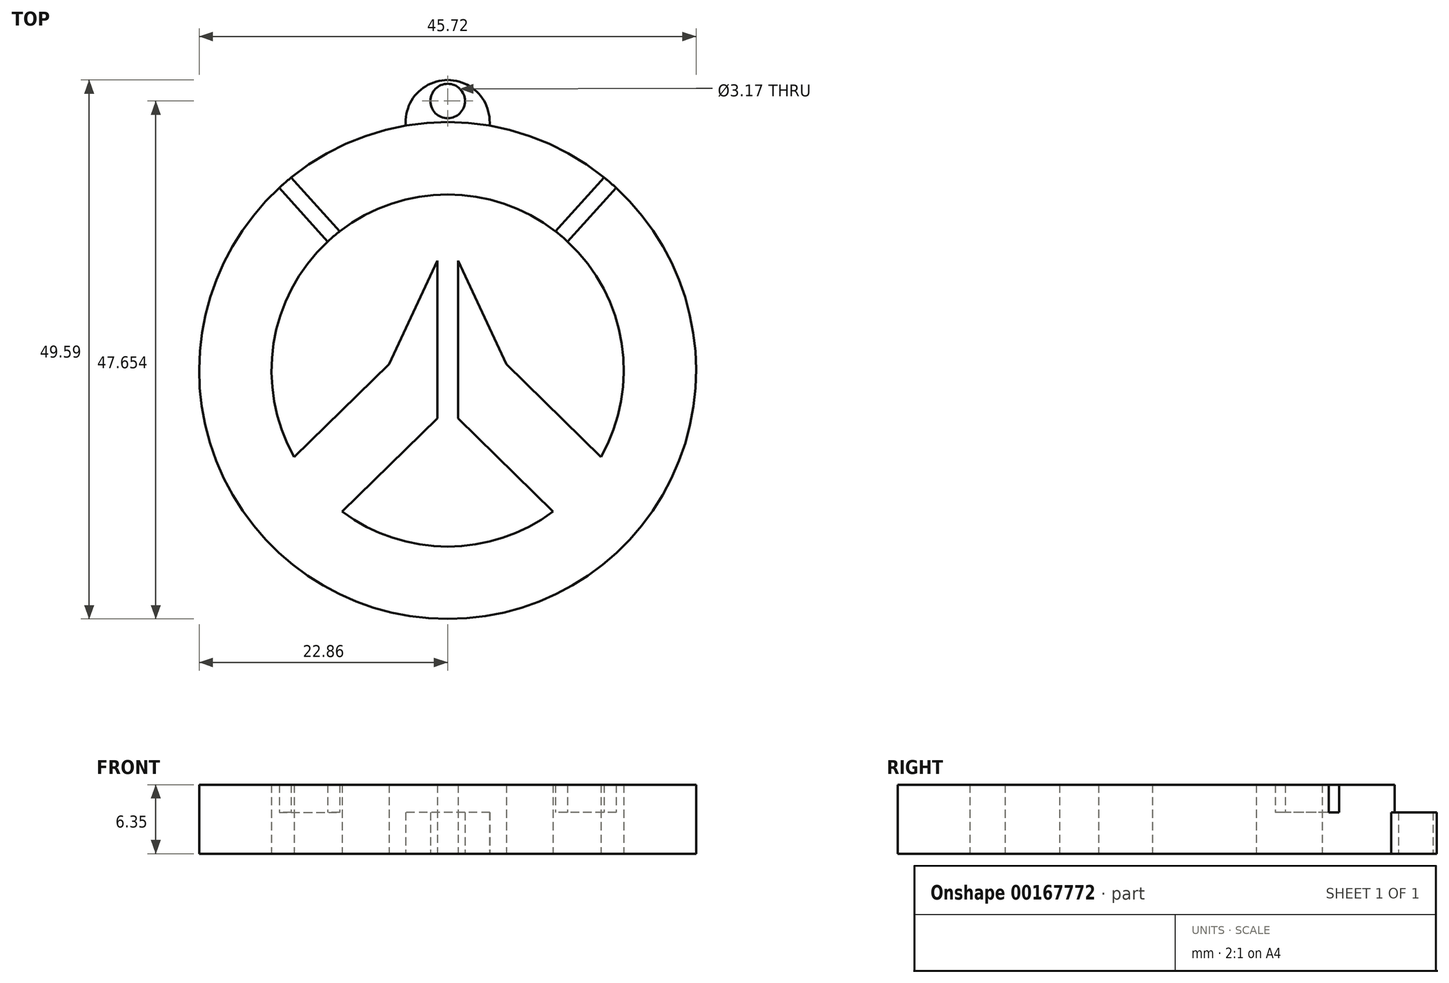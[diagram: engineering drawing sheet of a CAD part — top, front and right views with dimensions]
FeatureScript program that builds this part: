
annotation { "Feature Type Name" : "Feature", "Feature Type Description" : "" }
export const myFeature = defineFeature(function(context is Context, id is Id, definition is map)
    precondition{}
    {
        {
            var Q0;
            Q0=qCreatedBy(makeId("Top.planeOp"),FACE);
            var sketch = newSketch(context, id + "F0", { "sketchPlane" : qUnion([Q0])});
            skArc(sketch, "E0", {"start": v(-3.2, 22.5) * mm, "mid": v(-26.07, -0.35) * mm, "end": v(-3.2, -23.21) * mm});
            skArc(sketch, "E1", {"start": v(-3.2, 15.85) * mm, "mid": v(-17.2, 7.82) * mm, "end": v(-17.32, -8.32) * mm});
            skLineSegment(sketch, "E2", {"start": v(-4.15, 9.77) * mm, "end": v(-4.15, -4.75) * mm});
            skLineSegment(sketch, "E3", {"start": v(-4.15, -4.75) * mm, "end": v(-12.9, -13.33) * mm});
            skLineSegment(sketch, "E4", {"start": v(-17.32, -8.32) * mm, "end": v(-8.6, 0.23) * mm});
            skLineSegment(sketch, "E5", {"start": v(-8.6, 0.23) * mm, "end": v(-4.15, 9.77) * mm});
            skArc(sketch, "E6.trimOffspring", {"start": v(-12.9, -13.33) * mm, "mid": v(-8.32, -15.73) * mm, "end": v(-3.2, -16.56) * mm});
            skLineSegment(sketch, "E7", {"start": v(-17.61, 17.4) * mm, "end": v(-13.14, 12.46) * mm});
            skLineSegment(sketch, "E8", {"start": v(-18.71, 16.45) * mm, "end": v(-14.25, 11.51) * mm});
            skArc(sketch, "E9.MirrorCS", {"start": v(-3.2, 22.5) * mm, "mid": v(19.65, -0.35) * mm, "end": v(-3.2, -23.21) * mm});
            skArc(sketch, "E10.MirrorCS", {"start": v(-3.2, 15.85) * mm, "mid": v(10.79, 7.82) * mm, "end": v(10.9, -8.32) * mm});
            skLineSegment(sketch, "E11.MirrorCS", {"start": v(11.2, 17.4) * mm, "end": v(6.72, 12.46) * mm});
            skLineSegment(sketch, "E12.MirrorCS", {"start": v(12.3, 16.45) * mm, "end": v(7.83, 11.51) * mm});
            skLineSegment(sketch, "E13.MirrorCS", {"start": v(-2.27, -4.75) * mm, "end": v(6.49, -13.33) * mm});
            skLineSegment(sketch, "E14.MirrorCS", {"start": v(-2.27, 9.77) * mm, "end": v(-2.27, -4.75) * mm});
            skLineSegment(sketch, "E15.MirrorCS", {"start": v(2.18, 0.23) * mm, "end": v(-2.27, 9.77) * mm});
            skLineSegment(sketch, "E16.MirrorCS", {"start": v(10.9, -8.32) * mm, "end": v(2.18, 0.23) * mm});
            skArc(sketch, "E17.MirrorCS", {"start": v(6.49, -13.33) * mm, "mid": v(1.9, -15.73) * mm, "end": v(-3.2, -16.56) * mm});
            skArc(sketch, "E18", {"start": v(0.65, 22.18) * mm, "mid": v(-3.2, 26.38) * mm, "end": v(-7.07, 22.18) * mm});
            skCircle(sketch, "E19", {"center": v(-3.2, 24.44) * mm, "radius": 1.59 * mm});
            skSolve(sketch);
        }
        {
            var Q0;
            {var subQ4=sQuery(id+"F0.wireOp",EDGE,"E7");Q0=makeQuery(id+"F0.imprint","IMPRINT",FACE,{"disambiguationData":[TD([[makeQuery(id+"F0.imprint","IMPRINT",EDGE,{"derivedFrom":subQ4}),1.0]])]});}
            var Q1;
            Q1=makeQuery(id+"F0.imprint","IMPRINT",FACE,{"disambiguationData":[TD([[makeQuery(id+"F0.imprint","IMPRINT",EDGE,{"derivedFrom":sQuery(id+"F0.wireOp",EDGE,"E2")}),-1.0]])]});
            extrude(context, id + "F1", {"entities" : qUnion([Q0, Q1]), "depth" : 6.35 * mm});
        }
        {
            var Q0;
            {var subQ3=sQuery(id+"F0.wireOp",EDGE,"E18");Q0=makeQuery(id+"F0.imprint","IMPRINT",FACE,{"disambiguationData":[TD([[makeQuery(id+"F0.imprint","IMPRINT",EDGE,{"derivedFrom":subQ3}),1.0]])]});}
            var Q1;
            {var subQ0=sQuery(id+"F0.wireOp",EDGE,"E11.MirrorCS");Q1=makeQuery(id+"F0.imprint","IMPRINT",FACE,{"disambiguationData":[TD([[makeQuery(id+"F0.imprint","IMPRINT",EDGE,{"derivedFrom":subQ0}),1.0]])]});}
            var Q2;
            {var subQ0=sQuery(id+"F0.wireOp",EDGE,"E7");Q2=makeQuery(id+"F0.imprint","IMPRINT",FACE,{"disambiguationData":[TD([[makeQuery(id+"F0.imprint","IMPRINT",EDGE,{"derivedFrom":subQ0}),-1.0]])]});}
            extrude(context, id + "F2", {"entities" : qUnion([Q0, Q1, Q2]), "operationType" : NewBodyOperationType.ADD, "depth" : 3.8 * mm});
        }
    });
